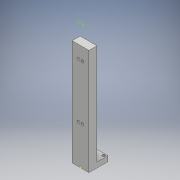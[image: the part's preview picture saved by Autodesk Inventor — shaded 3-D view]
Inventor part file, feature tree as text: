
AUTODESK INVENTOR PART (.ipt)
format: ipt  version: 2017.3 (Build 213256000, 256)  size: 133,632 bytes
history: native  units: mm
features: sketch x7, extrude x4, hole x2, pattern_linear x1
ambient origin geometry x8: Origin, YZ Plane, XZ Plane, XY Plane, X Axis, Y Axis, Z Axis, Center Point
bodies: Solid1 (feature_tree)
feature tree (14):
  extrude  "Extrusion1"  Depth=22.525mm
  extrude  "Extrusion2"  Depth=120.0mm TaperAngle=0.0deg
  hole  "Hole2"  [1 undecoded]
  extrude  "Extrusion3"  Depth=20.0mm
  sketch  "Sketch6"  dims[d61=19.7mm d62=0.0mm]
  hole  "Hole5"  [1 undecoded]
  pattern_linear  "Rectangular Pattern4"  [2 undecoded]
  extrude  "Extrusion4"  [1 undecoded]
  sketch  "Sketch1"  dims[d0=20.0mm d1=22.525mm]
  sketch  "Sketch2"  dims[d2=6.35mm d3=0.0mm d4=120.0mm d5=0.0mm]
  sketch  "Sketch4"  dims[d19=3.175mm d20=6.0mm d21=4.0mm d22=2.0mm d23=90.0deg d24=12.0mm d25=20.594885mm d39=3.175mm d40=0.0mm]
  sketch  "Sketch5"  dims[d51=3.175mm d52=10.973mm d53=4.0mm d54=2.0mm d55=90.0deg d56=16.265mm d57=20.594885mm d58=20.0mm d60=65.0mm]
  sketch  "Sketch7"
  sketch  "Sketch8"
note: 5 required parameter values undecoded (feature->parameter linkage not recoverable at this tier; creation-order binding heuristic only, values carry confidence <= 0.55)
